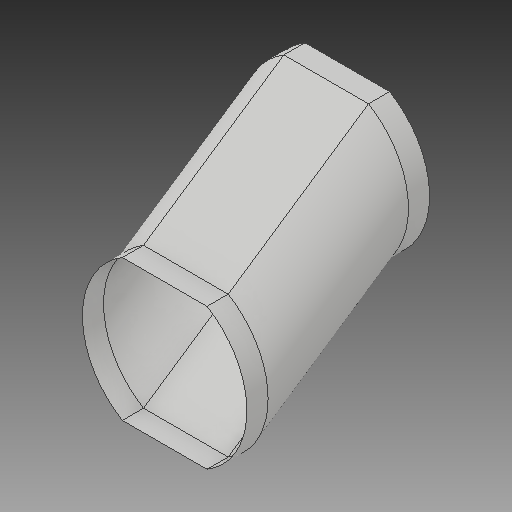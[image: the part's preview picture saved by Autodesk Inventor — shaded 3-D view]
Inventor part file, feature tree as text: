
AUTODESK INVENTOR PART (.ipt)
format: ipt  version: 2017 (Build 210142000, 142)  size: 150,528 bytes
history: native  units: in
note: dims shown in document units (in); Inventor stores cm internally (conversion verified against a paired STEP export)
features: sketch x2, extrude x2, plane x1, sweep x1, delete_face x1
ambient origin geometry x8: Origin, YZ Plane, XZ Plane, XY Plane, X Axis, Y Axis, Z Axis, Center Point
bodies: Solid1 (feature_tree)
feature tree (7):
  sketch  "Sketch1"  dims[d0=6.6667in d3=1.0in d4=0.0in d12=8.0in]
  extrude  "connection top"  Depth=8.0in
  plane  "Work Plane2"
  sweep  "ramp"
  extrude  "connection bottom"  Depth=3.8873in TaperAngle=0.0deg
  delete_face  "Delete Face1"
  sketch  "Sketch6"  dims[d28=8.0in d45=0.0in d46=0.0in d49=1.0in d50=0.0in d70=0.8521in d87=4.0in d89=3.8873in d90=3.8873in d94=1.6458in d100=3.3333in d102=4.0in d104=3.8873in d105=3.8873in d109=1.6458in d115=3.3333in]
